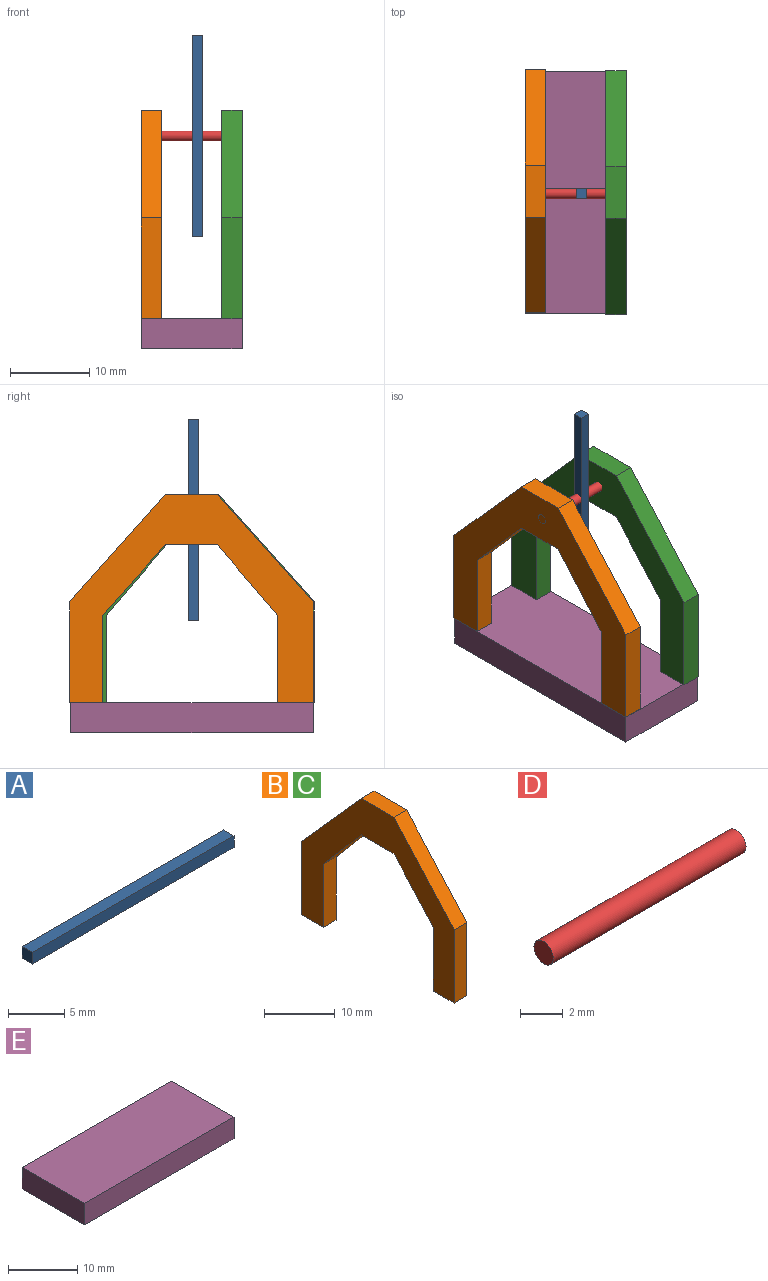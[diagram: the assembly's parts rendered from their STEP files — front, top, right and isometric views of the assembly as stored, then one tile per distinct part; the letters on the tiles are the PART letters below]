
ASSEMBLY  parts=5 mates=3
PART A: 6 faces, bbox 25.4x1.3x1.3 mm
  f0: plane 25.4x1.27mm, normal (0,0,1), area 32.3mm2, adj f1,f3,f4,f5
  f1: plane 1.27x1.27mm, normal (-1,0,0), area 1.6mm2, adj f0,f2,f4,f5
  f2: plane 25.4x1.27mm, normal (0,0,-1), area 32.3mm2, adj f1,f3,f4,f5
  f3: plane 1.27x1.27mm, normal (1,0,0), area 1.6mm2, adj f0,f2,f4,f5
  f4: plane 25.4x1.27mm, normal (0,-1,0), area 32.3mm2, adj f0,f1,f2,f3
  f5: plane 25.4x1.27mm, normal (0,1,0), area 32.3mm2, adj f0,f1,f2,f3
PART B: 14 faces, bbox 2.5x30.7x26.2 mm
  f0: plane 12.68x2.54mm, normal (0,-1,0), area 32.2mm2, adj f1,f11,f12,f13
  f1: plane 4.14x2.54mm, normal (0,0,-1), area 10.5mm2, adj f0,f2,f12,f13
  f2: plane 10.99x2.54mm, normal (0,1,0), area 27.9mm2, adj f1,f3,f12,f13
  f3: plane 8.88x7.91mm, normal (0,0.75,-0.67), area 30.2mm2, adj f2,f4,f12,f13
  f4: plane 6.55x2.54mm, normal (0,0,-1), area 16.6mm2, adj f3,f5,f12,f13
  f5: plane 8.88x7.61mm, normal (0,-0.76,-0.65), area 29.7mm2, adj f4,f6,f12,f13
  f6: plane 10.99x2.54mm, normal (0,-1,0), area 27.9mm2, adj f5,f7,f12,f13
  f7: plane 4.44x2.54mm, normal (0,0,-1), area 11.3mm2, adj f6,f8,f12,f13
  f8: plane 12.68x2.54mm, normal (0,1,0), area 32.2mm2, adj f7,f9,f12,f13
  f9: plane 13.53x12.05mm, normal (0,0.75,0.67), area 46mm2, adj f8,f10,f12,f13
  f10: plane 6.55x2.54mm, normal (0,0,1), area 16.6mm2, adj f9,f11,f12,f13
  f11: plane 13.53x12.05mm, normal (0,-0.75,0.67), area 46mm2, adj f0,f10,f12,f13
  f12: plane 30.65x26.21mm, normal (1,0,0), area 270.8mm2, adj f0,f1,f2,f3,f4,f5,f6,f7
  f13: plane 30.65x26.21mm, normal (-1,0,0), area 270.8mm2, adj f0,f1,f2,f3,f4,f5,f6,f7
PART C: same geometry as B
PART D: 3 faces, bbox 12.7x1.3x1.3 mm
  f0: cylinder r=0.64mm len=12.7mm, axis (-1,0,0), area 50.7mm2, adj f1,f2
  f1: plane 1.27x1.27mm, normal (1,0,0), area 1.3mm2, adj f0
  f2: plane 1.27x1.27mm, normal (-1,0,0), area 1.3mm2, adj f0
PART E: 6 faces, bbox 30.5x12.7x3.8 mm
  f0: plane 12.7x3.81mm, normal (-1,0,0), area 48.4mm2, adj f1,f3,f4,f5
  f1: plane 30.48x3.81mm, normal (0,-1,0), area 116.1mm2, adj f0,f2,f4,f5
  f2: plane 12.7x3.81mm, normal (1,0,0), area 48.4mm2, adj f1,f3,f4,f5
  f3: plane 30.48x3.81mm, normal (0,1,0), area 116.1mm2, adj f0,f2,f4,f5
  f4: plane 30.48x12.7mm, normal (0,0,1), area 387.1mm2, adj f0,f1,f2,f3
  f5: plane 30.48x12.7mm, normal (0,0,-1), area 387.1mm2, adj f0,f1,f2,f3
PLACE A rot(axis=(0,-1,0),90deg) t=(64.81,17.07,56.51)mm
PLACE B rot(axis=(0,0,1),180deg) t=(9.52,-8.92,-4.33)mm
PLACE C t=(17.14,42.27,-4.33)mm
PLACE D t=(7.07,-3.57,-3.46)mm
PLACE E rot(axis=(0,0,-1),90deg) t=(6.98,31.91,-8.14)mm
MATE fastened B.f7 <-> E.f4  axis (0,0,-1) through (6.98,1.43,-4.33)mm
MATE fastened A.f0 <-> D.f0  axis (-1,0,0) through (13.42,16.43,18.67)mm
MATE fastened E.f4 <-> C.f7  axis (0,0,1) through (19.68,31.91,-4.33)mm
